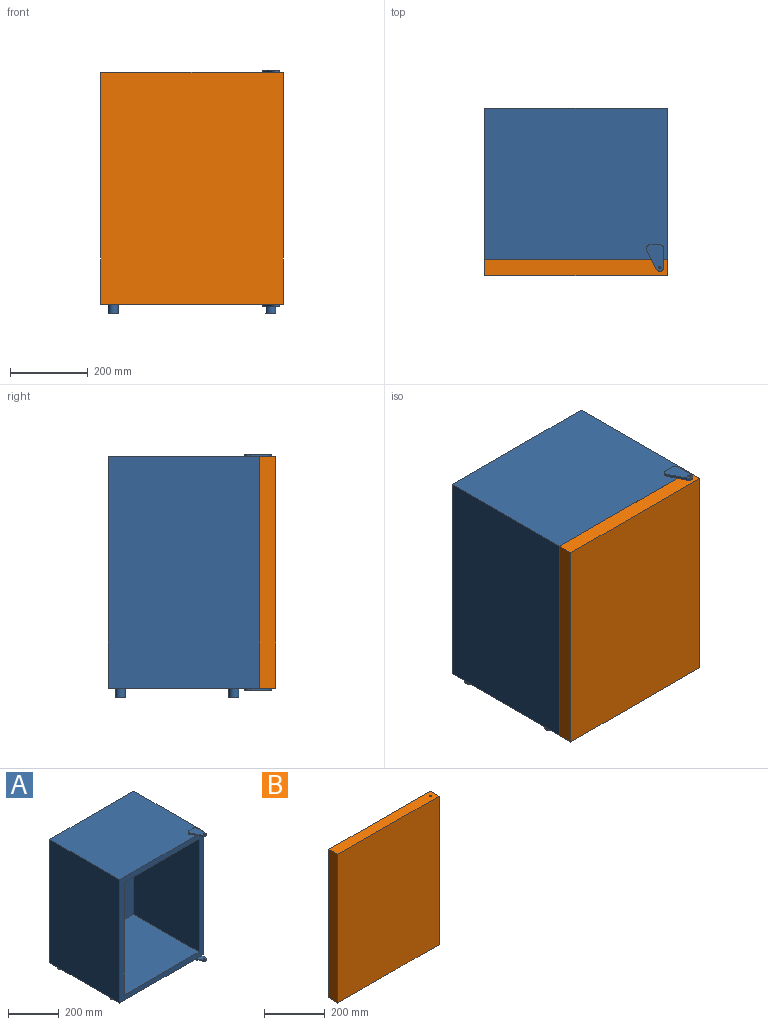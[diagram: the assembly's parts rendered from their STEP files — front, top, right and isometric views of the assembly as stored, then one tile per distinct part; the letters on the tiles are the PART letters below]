
ASSEMBLY  parts=2 mates=1
PART A: 37 faces, bbox 469.9x420.7x628.7 mm
  f0: plane 596.9x469.9mm, normal (0,-1,0), area 51612.8mm2, adj f1,f3,f4,f5,f6,f8,f9,f10
  f1: plane 596.9x390.53mm, normal (1,0,0), area 233104.4mm2, adj f0,f2,f4,f5
  f2: plane 596.9x469.9mm, normal (0,1,0), area 280483.3mm2, adj f1,f3,f4,f5
  f3: plane 596.9x390.53mm, normal (-1,0,0), area 233104.4mm2, adj f0,f2,f4,f5
  f4: plane 469.9x390.53mm, normal (0,0,1), area 182025.5mm2, adj f0,f1,f2,f3,f30,f32,f33,f35
  f5: plane 469.9x390.53mm, normal (0,0,-1), area 179998.6mm2, adj f0,f1,f2,f3,f11,f13,f15,f17
  f6: plane 546.1x365.13mm, normal (-1,0,0), area 199394.8mm2, adj f0,f7,f9,f10
  f7: plane 546.1x419.1mm, normal (0,-1,0), area 228870.5mm2, adj f6,f8,f9,f10
  f8: plane 546.1x365.13mm, normal (1,0,0), area 199394.8mm2, adj f0,f7,f9,f10
  f9: plane 419.1x365.13mm, normal (0,0,-1), area 153023.9mm2, adj f0,f6,f7,f8
  f10: plane 419.1x365.13mm, normal (0,0,1), area 153023.9mm2, adj f0,f6,f7,f8
  f11: cylinder r=12.7mm len=25.4mm, axis (0,0,-1), area 2026.8mm2, adj f5,f12
  f12: plane 25.4x25.4mm, normal (0,0,-1), area 506.7mm2, adj f11
  f13: cylinder r=12.7mm len=25.4mm, axis (0,0,-1), area 2026.8mm2, adj f5,f14
  f14: plane 25.4x25.4mm, normal (0,0,-1), area 506.7mm2, adj f13
  f15: cylinder r=12.7mm len=25.4mm, axis (0,0,-1), area 2026.8mm2, adj f5,f16
  f16: plane 25.4x25.4mm, normal (0,0,-1), area 506.7mm2, adj f15
  f17: cylinder r=12.7mm len=25.4mm, axis (0,0,-1), area 2026.8mm2, adj f5,f18
  f18: plane 25.4x25.4mm, normal (0,0,-1), area 506.7mm2, adj f17
  f19: plane 30.99x30.16mm, normal (0,0,1), area 641.5mm2, adj f0,f21,f22,f23,f27
  f20: plane 68.26x44.64mm, normal (0,0,-1), area 2123.7mm2, adj f21,f22,f23,f24,f25,f26,f27
  f21: cylinder r=9.53mm len=17.98mm, axis (0,0,-1), area 161mm2, adj f19,f20,f22,f23
  f22: plane 49.21x25.59mm, normal (-0.89,-0.46,0), area 352.2mm2, adj f5,f19,f20,f21,f24
  f23: plane 49.21x6.35mm, normal (1,0,0), area 312.5mm2, adj f5,f19,f20,f21,f25
  f24: cylinder r=9.53mm len=13.92mm, axis (0,0,-1), area 124mm2, adj f5,f20,f22,f26
  f25: cylinder r=9.53mm len=9.53mm, axis (0,0,-1), area 95mm2, adj f5,f20,f23,f26
  f26: plane 25.59x6.35mm, normal (0,1,0), area 162.5mm2, adj f5,f20,f24,f25
  f27: cylinder r=3.17mm len=6.35mm, axis (0,0,-1), area 126.7mm2, adj f19,f20
  f28: plane 30.99x30.16mm, normal (0,0,-1), area 641.5mm2, adj f0,f30,f31,f32,f34
  f29: plane 68.26x44.64mm, normal (0,0,1), area 2123.7mm2, adj f30,f31,f32,f33,f34,f35,f36
  f30: plane 49.21x25.59mm, normal (-0.89,-0.46,0), area 352.2mm2, adj f4,f28,f29,f31,f33
  f31: cylinder r=9.53mm len=17.98mm, axis (0,0,-1), area 161mm2, adj f28,f29,f30,f32
  f32: plane 49.21x6.35mm, normal (1,0,0), area 312.5mm2, adj f4,f28,f29,f31,f35
  f33: cylinder r=9.53mm len=13.92mm, axis (0,0,-1), area 124mm2, adj f4,f29,f30,f36
  f34: cylinder r=3.17mm len=6.35mm, axis (0,0,-1), area 126.7mm2, adj f28,f29
  f35: cylinder r=9.53mm len=9.53mm, axis (0,0,-1), area 95mm2, adj f4,f29,f32,f36
  f36: plane 25.59x6.35mm, normal (0,1,0), area 162.5mm2, adj f4,f29,f33,f35
PART B: 7 faces, bbox 469.9x41.3x596.9 mm
  f0: plane 469.9x41.28mm, normal (0,0,1), area 19363.5mm2, adj f1,f2,f4,f5,f6
  f1: plane 596.9x469.9mm, normal (0,1,0), area 280483.3mm2, adj f0,f2,f3,f5
  f2: plane 596.9x41.28mm, normal (1,0,0), area 24637mm2, adj f0,f1,f3,f6
  f3: plane 469.9x41.28mm, normal (0,0,-1), area 19363.5mm2, adj f1,f2,f4,f5,f6
  f4: cylinder r=3.17mm len=596.9mm, axis (0,0,-1), area 11907.6mm2, adj f0,f3
  f5: plane 596.9x41.28mm, normal (-1,0,0), area 24637mm2, adj f0,f1,f3,f6
  f6: plane 596.9x469.9mm, normal (0,-1,0), area 280483.3mm2, adj f0,f2,f3,f5
PLACE A t=(-469.9,0,-25.4)mm
PLACE B rot(axis=(0,0,1),0deg) t=(-469.9,0,-25.4)mm
MATE revolute B.f4 <-> A.f21  axis (0,0,1) through (-19.05,-411.16,596.9)mm
